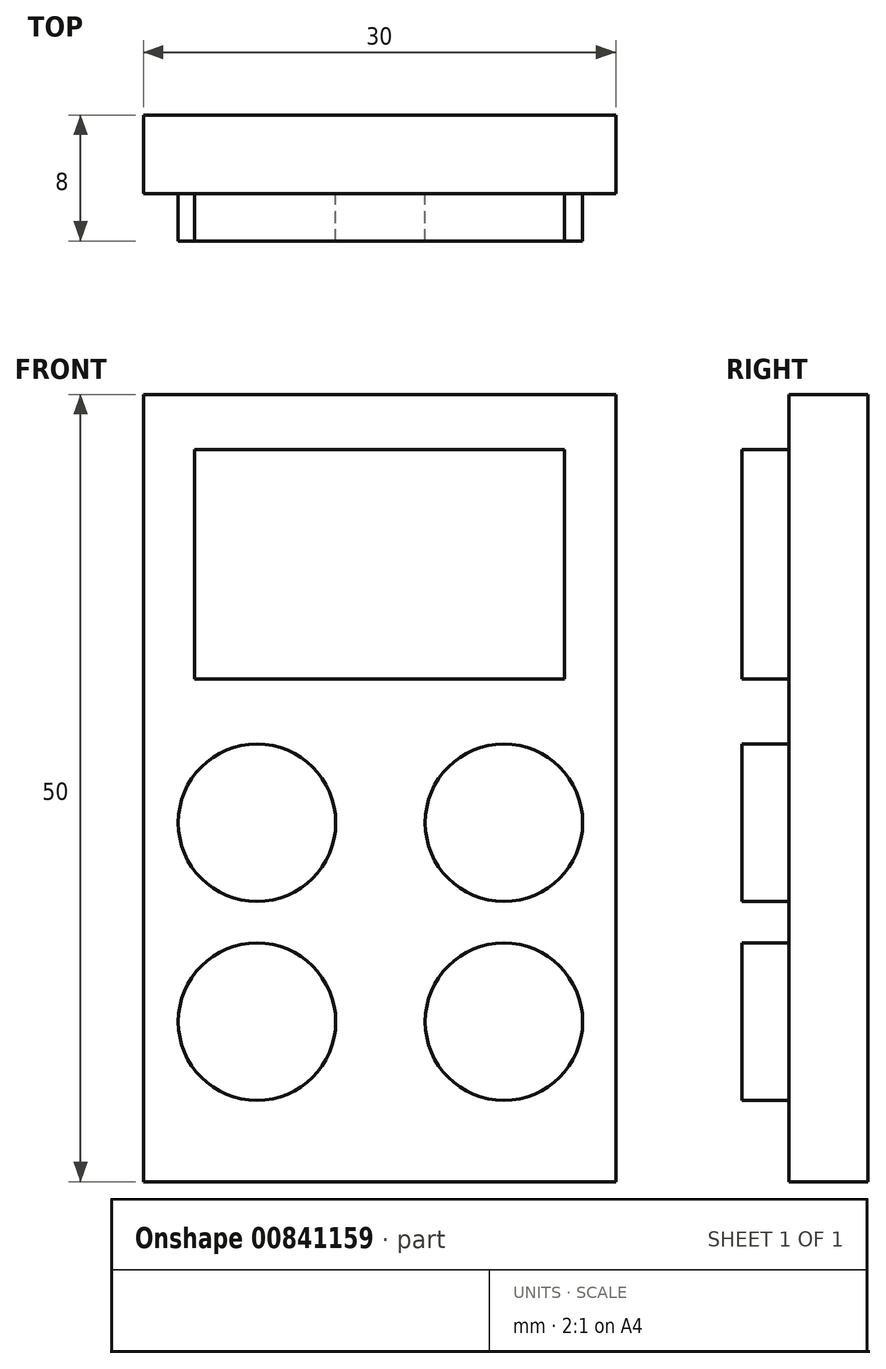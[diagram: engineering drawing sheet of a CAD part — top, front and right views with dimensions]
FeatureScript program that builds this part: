
annotation { "Feature Type Name" : "Feature", "Feature Type Description" : "" }
export const myFeature = defineFeature(function(context is Context, id is Id, definition is map)
    precondition{}
    {
        {
            var Q0;
            Q0=qCreatedBy(makeId("Front.planeOp"),FACE);
            var sketch = newSketch(context, id + "F0", { "sketchPlane" : qUnion([Q0])});
            skLineSegment(sketch, "E0.bottom", {"start": v(-15, 25) * mm, "end": v(15, 25) * mm});
            skLineSegment(sketch, "E0.top", {"start": v(-15, -25) * mm, "end": v(15, -25) * mm});
            skLineSegment(sketch, "E0.left", {"start": v(-15, 25) * mm, "end": v(-15, -25) * mm});
            skLineSegment(sketch, "E0.right", {"start": v(15, 25) * mm, "end": v(15, -25) * mm});
            skPoint(sketch, "E0.middle", {"position": v(0, 0) * mm});
            skSolve(sketch);
        }
        {
            var Q0;
            Q0=makeQuery(id+"F0.imprint","IMPRINT",FACE,{"disambiguationData":[TD([[makeQuery(id+"F0.imprint","IMPRINT",EDGE,{"derivedFrom":sQuery(id+"F0.wireOp",EDGE,"E0.bottom")}),-1.0]])]});
            extrude(context, id + "F1", {"entities" : qUnion([Q0]), "depth" : 5 * mm, "offsetDistance" : 25 * mm});
        }
        {
            var Q0;
            Q0=makeQuery(id+"F1.opExtrude","CAP_FACE",FACE,{"disambiguationData":[OSD([sQuery(id+"F0.wireOp",EDGE,"E0.bottom"),sQuery(id+"F0.wireOp",EDGE,"E0.top"),sQuery(id+"F0.wireOp",EDGE,"E0.left"),sQuery(id+"F0.wireOp",EDGE,"E0.right")])],"isStart":false});
            var sketch = newSketch(context, id + "F2", { "sketchPlane" : qUnion([Q0])});
            skLineSegment(sketch, "E1.bottom", {"start": v(-11.76, 6.94) * mm, "end": v(11.76, 6.94) * mm});
            skLineSegment(sketch, "E1.top", {"start": v(-11.76, 21.5) * mm, "end": v(11.76, 21.5) * mm});
            skLineSegment(sketch, "E1.left", {"start": v(-11.76, 6.94) * mm, "end": v(-11.76, 21.5) * mm});
            skLineSegment(sketch, "E1.right", {"start": v(11.76, 6.94) * mm, "end": v(11.76, 21.5) * mm});
            skPoint(sketch, "E1.middle", {"position": v(0, 14.22) * mm});
            skCircle(sketch, "E2", {"center": v(-7.79, -2.2) * mm, "radius": 5 * mm});
            skCircle(sketch, "E3", {"center": v(7.9, -2.2) * mm, "radius": 5 * mm});
            skCircle(sketch, "E4", {"center": v(7.9, -14.84) * mm, "radius": 5 * mm});
            skCircle(sketch, "E5", {"center": v(-7.79, -14.84) * mm, "radius": 5 * mm});
            skSolve(sketch);
        }
        {
            var Q0;
            Q0=makeQuery(id+"F2.imprint","IMPRINT",FACE,{"disambiguationData":[TD([[makeQuery(id+"F2.imprint","IMPRINT",EDGE,{"derivedFrom":sQuery(id+"F2.wireOp",EDGE,"E1.bottom")}),1.0]])]});
            var Q1;
            Q1=makeQuery(id+"F2.imprint","IMPRINT",FACE,{"disambiguationData":[TD([[makeQuery(id+"F2.imprint","IMPRINT",EDGE,{"derivedFrom":sQuery(id+"F2.wireOp",EDGE,"E2")}),1.0]])]});
            var Q2;
            Q2=makeQuery(id+"F2.imprint","IMPRINT",FACE,{"disambiguationData":[TD([[makeQuery(id+"F2.imprint","IMPRINT",EDGE,{"derivedFrom":sQuery(id+"F2.wireOp",EDGE,"E3")}),1.0]])]});
            var Q3;
            Q3=makeQuery(id+"F2.imprint","IMPRINT",FACE,{"disambiguationData":[TD([[makeQuery(id+"F2.imprint","IMPRINT",EDGE,{"derivedFrom":sQuery(id+"F2.wireOp",EDGE,"E5")}),1.0]])]});
            var Q4;
            Q4=makeQuery(id+"F2.imprint","IMPRINT",FACE,{"disambiguationData":[TD([[makeQuery(id+"F2.imprint","IMPRINT",EDGE,{"derivedFrom":sQuery(id+"F2.wireOp",EDGE,"E4")}),1.0]])]});
            extrude(context, id + "F3", {"entities" : qUnion([Q0, Q1, Q2, Q3, Q4]), "operationType" : NewBodyOperationType.ADD, "depth" : 3 * mm, "offsetDistance" : 25 * mm});
        }
    });
